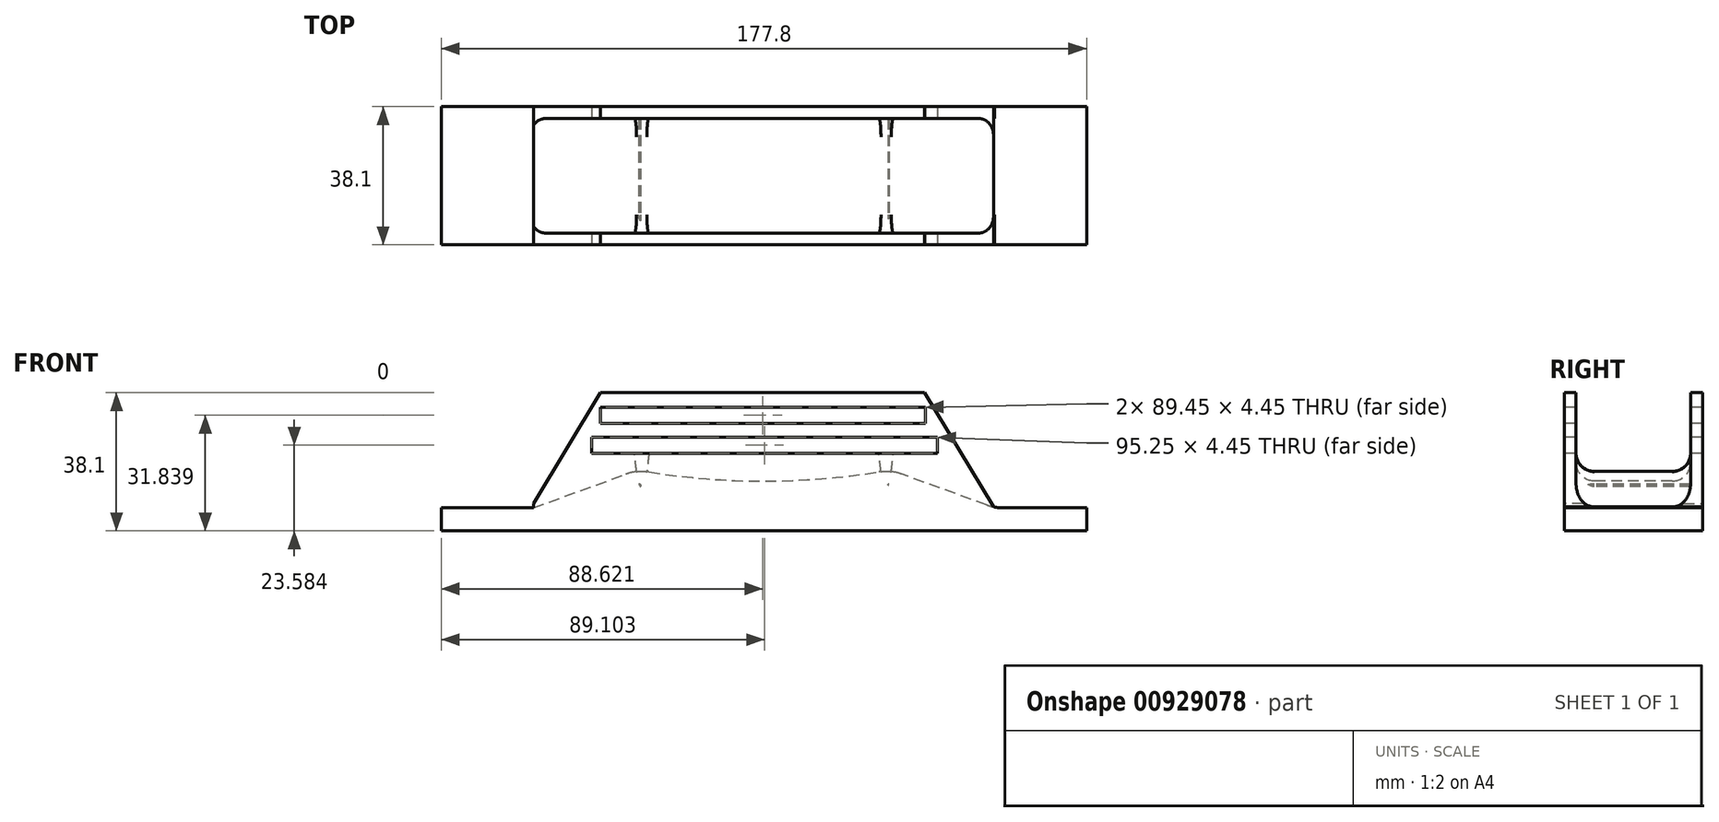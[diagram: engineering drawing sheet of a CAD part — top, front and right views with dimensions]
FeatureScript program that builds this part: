
annotation { "Feature Type Name" : "Feature", "Feature Type Description" : "" }
export const myFeature = defineFeature(function(context is Context, id is Id, definition is map)
    precondition{}
    {
        {
            var Q0;
            Q0=qCreatedBy(makeId("Top.planeOp"),FACE);
            var sketch = newSketch(context, id + "F0", { "sketchPlane" : qUnion([Q0])});
            skLineSegment(sketch, "E0.bottom", {"start": v(-37.6, 21.46) * mm, "end": v(140.2, 21.46) * mm});
            skLineSegment(sketch, "E0.top", {"start": v(-37.6, -16.64) * mm, "end": v(140.2, -16.64) * mm});
            skLineSegment(sketch, "E0.left", {"start": v(-37.6, 21.46) * mm, "end": v(-37.6, -16.64) * mm});
            skLineSegment(sketch, "E0.right", {"start": v(140.2, 21.46) * mm, "end": v(140.2, -16.64) * mm});
            skSolve(sketch);
        }
        {
            var Q0;
            Q0 = qSketchRegion(id + "F0", true);
            extrude(context, id + "F1", {"entities" : qUnion([Q0]), "depth" : 6.35 * mm, "offsetDistance" : 25.4 * mm});
        }
        {
            var Q0;
            Q0=makeQuery(id+"F1.opExtrude","SWEPT_FACE",FACE,{"disambiguationData":[OSD([sQuery(id+"F0.wireOp",EDGE,"E0.top")])]});
            var sketch = newSketch(context, id + "F2", { "sketchPlane" : qUnion([Q0])});
            skLineSegment(sketch, "E1", {"start": v(-12.2, 6.35) * mm, "end": v(16.44, 16.77) * mm});
            skLineSegment(sketch, "E2", {"start": v(114.8, 6.35) * mm, "end": v(86.15, 16.77) * mm});
            skLineSegment(sketch, "E3", {"start": v(16.44, 16.77) * mm, "end": v(17.74, 13.2) * mm});
            skLineSegment(sketch, "E4", {"start": v(17.74, 13.2) * mm, "end": v(-1.06, 6.35) * mm});
            skLineSegment(sketch, "E5", {"start": v(86.15, 16.77) * mm, "end": v(84.85, 13.2) * mm});
            skLineSegment(sketch, "E6", {"start": v(84.85, 13.2) * mm, "end": v(103.66, 6.35) * mm});
            skSolve(sketch);
        }
        {
            var Q0;
            {var subQ0=sQuery(id+"F0.wireOp",EDGE,"E0.top");Q0=makeQuery(id+"F4.boolean.opBoolean","MERGE",FACE,{"derivedFrom":[makeQuery(id+"F1.opExtrude","SWEPT_FACE",FACE,{"disambiguationData":[OSD([subQ0])]}),makeQuery(id+"F4.opExtrude","CAP_FACE",FACE,{"disambiguationData":[OSD([subQ0,sQuery(id+"F2.wireOp",EDGE,"E1"),sQuery(id+"F2.wireOp",EDGE,"E3"),sQuery(id+"F2.wireOp",EDGE,"E4")])],"isStart":true}),makeQuery(id+"F4.opExtrude","CAP_FACE",FACE,{"disambiguationData":[OSD([subQ0,sQuery(id+"F2.wireOp",EDGE,"E2"),sQuery(id+"F2.wireOp",EDGE,"E5"),sQuery(id+"F2.wireOp",EDGE,"E6")])],"isStart":true})]});}
            var sketch = newSketch(context, id + "F3", { "sketchPlane" : qUnion([Q0])});
            skArc(sketch, "E7", {"start": v(16.44, 16.77) * mm, "mid": v(51.3, 13.7) * mm, "end": v(86.15, 16.77) * mm});
            skLineSegment(sketch, "E8", {"start": v(16.44, 16.77) * mm, "end": v(16.44, 12.96) * mm});
            skLineSegment(sketch, "E9", {"start": v(86.15, 16.77) * mm, "end": v(86.15, 12.96) * mm});
            skArc(sketch, "E10", {"start": v(16.44, 12.96) * mm, "mid": v(51.3, 9.18) * mm, "end": v(86.15, 12.96) * mm});
            skSolve(sketch);
        }
        {
            var Q0;
            {var subQ0=sQuery(id+"F2.wireOp",EDGE,"E1");Q0=makeQuery(id+"F2.imprint","IMPRINT",FACE,{"disambiguationData":[TD([[makeQuery(id+"F2.imprint","IMPRINT",EDGE,{"derivedFrom":subQ0}),-1.0]])]});}
            var Q1;
            {var subQ0=sQuery(id+"F2.wireOp",EDGE,"E2");Q1=makeQuery(id+"F2.imprint","IMPRINT",FACE,{"disambiguationData":[TD([[makeQuery(id+"F2.imprint","IMPRINT",EDGE,{"derivedFrom":subQ0}),1.0]])]});}
            var Q2;
            Q2=makeQuery(id+"F3.imprint","IMPRINT",FACE,{"disambiguationData":[TD([[makeQuery(id+"F3.imprint","IMPRINT",EDGE,{"derivedFrom":sQuery(id+"F3.wireOp",EDGE,"E7")}),-1.0]])]});
            extrude(context, id + "F4", {"entities" : qUnion([Q0, Q1, Q2]), "operationType" : NewBodyOperationType.ADD, "oppositeDirection" : true, "depth" : 38.1 * mm, "offsetDistance" : 25.4 * mm});
        }
        {
            var Q0;
            Q0=makeQuery(id+"F4.opExtrude","SWEPT_EDGE",EDGE,{"disambiguationData":[OSD([sQuery(id+"F0.wireOp",EDGE,"E0.top"),sQuery(id+"F2.wireOp",EDGE,"E1")])]});
            var Q1;
            Q1=makeQuery(id+"F4.opExtrude","SWEPT_EDGE",EDGE,{"disambiguationData":[OSD([sQuery(id+"F0.wireOp",EDGE,"E0.top"),sQuery(id+"F2.wireOp",EDGE,"E2")])]});
            var Q2;
            Q2=makeQuery(id+"F4.opExtrude","SWEPT_EDGE",EDGE,{"disambiguationData":[OSD([sQuery(id+"F0.wireOp",EDGE,"E0.top"),sQuery(id+"F2.wireOp",EDGE,"E6")])]});
            var Q3;
            Q3=makeQuery(id+"F4.opExtrude","SWEPT_EDGE",EDGE,{"disambiguationData":[OSD([sQuery(id+"F0.wireOp",EDGE,"E0.top"),sQuery(id+"F2.wireOp",EDGE,"E4")])]});
            var Q4;
            Q4=makeQuery(id+"F4.boolean.opBoolean","MERGE",EDGE,{"derivedFrom":[makeQuery(id+"F4.opExtrude","SWEPT_EDGE",EDGE,{"disambiguationData":[OSD([sQuery(id+"F2.wireOp",EDGE,"E2"),sQuery(id+"F2.wireOp",EDGE,"E5")])]}),makeQuery(id+"F4.opExtrude","SWEPT_EDGE",EDGE,{"disambiguationData":[OSD([sQuery(id+"F3.wireOp",EDGE,"E7"),sQuery(id+"F3.wireOp",EDGE,"E9")])]})]});
            var Q5;
            Q5=makeQuery(id+"F4.boolean.opBoolean","MERGE",EDGE,{"derivedFrom":[makeQuery(id+"F4.opExtrude","SWEPT_EDGE",EDGE,{"disambiguationData":[OSD([sQuery(id+"F2.wireOp",EDGE,"E1"),sQuery(id+"F2.wireOp",EDGE,"E3")])]}),makeQuery(id+"F4.opExtrude","SWEPT_EDGE",EDGE,{"disambiguationData":[OSD([sQuery(id+"F3.wireOp",EDGE,"E7"),sQuery(id+"F3.wireOp",EDGE,"E8")])]})]});
            fillet(context, id + "F5", {"entities" : qUnion([Q0, Q1, Q2, Q3, Q4, Q5]), "radius" : 12.7 * mm, "tangentPropagation" : true, "allowEdgeOverflow" : false});
        }
        {
            var Q0;
            Q0=qCreatedBy(makeId("Top.planeOp"),FACE);
            var sketch = newSketch(context, id + "F6", { "sketchPlane" : qUnion([Q0])});
            skLineSegment(sketch, "E11.bottom", {"start": v(-12.2, 21.46) * mm, "end": v(114.8, 21.46) * mm});
            skLineSegment(sketch, "E11.top", {"start": v(-12.2, 18.2) * mm, "end": v(114.8, 18.2) * mm});
            skLineSegment(sketch, "E11.left", {"start": v(-12.2, 21.46) * mm, "end": v(-12.2, 18.2) * mm});
            skLineSegment(sketch, "E11.right", {"start": v(114.8, 21.46) * mm, "end": v(114.8, 18.2) * mm});
            skLineSegment(sketch, "E12.bottom", {"start": v(-12.2, -16.64) * mm, "end": v(114.8, -16.64) * mm});
            skLineSegment(sketch, "E12.top", {"start": v(-12.2, -13.38) * mm, "end": v(114.8, -13.38) * mm});
            skLineSegment(sketch, "E12.left", {"start": v(-12.2, -16.64) * mm, "end": v(-12.2, -13.38) * mm});
            skLineSegment(sketch, "E12.right", {"start": v(114.8, -16.64) * mm, "end": v(114.8, -13.38) * mm});
            skSolve(sketch);
        }
        {
            var Q0;
            Q0 = qSketchRegion(id + "F6", true);
            extrude(context, id + "F7", {"entities" : qUnion([Q0]), "operationType" : NewBodyOperationType.ADD, "depth" : 38.1 * mm, "offsetDistance" : 25.4 * mm});
        }
        {
            var Q0;
            Q0=qCreatedBy(makeId("Front.planeOp"),FACE);
            var sketch = newSketch(context, id + "F8", { "sketchPlane" : qUnion([Q0])});
            skLineSegment(sketch, "E13", {"start": v(-12.75, 6.58) * mm, "end": v(6.3, 38.1) * mm});
            skLineSegment(sketch, "E14", {"start": v(6.3, 38.1) * mm, "end": v(95.55, 38.1) * mm});
            skLineSegment(sketch, "E15", {"start": v(95.55, 38.1) * mm, "end": v(114.6, 6.58) * mm});
            skLineSegment(sketch, "E16", {"start": v(114.6, 6.58) * mm, "end": v(148.12, 6.58) * mm});
            skLineSegment(sketch, "E17", {"start": v(148.12, 6.58) * mm, "end": v(104.98, 72.7) * mm});
            skLineSegment(sketch, "E18", {"start": v(104.98, 72.7) * mm, "end": v(-3.95, 64.2) * mm});
            skLineSegment(sketch, "E19", {"start": v(-3.95, 64.2) * mm, "end": v(-37.6, 6.36) * mm});
            skLineSegment(sketch, "E20", {"start": v(-37.6, 6.36) * mm, "end": v(-12.75, 6.58) * mm});
            skSolve(sketch);
        }
        {
            var Q0;
            Q0=makeQuery(id+"F8.imprint","IMPRINT",FACE,{"disambiguationData":[TD([[makeQuery(id+"F8.imprint","IMPRINT",EDGE,{"derivedFrom":sQuery(id+"F8.wireOp",EDGE,"E13")}),1.0]])]});
            extrude(context, id + "F9", {"entities" : qUnion([Q0]), "operationType" : NewBodyOperationType.REMOVE, "endBound" : BoundingType.SYMMETRIC, "oppositeDirection" : true, "depth" : 254 * mm, "offsetDistance" : 25.4 * mm});
        }
        {
            var Q0;
            {var subQ0=sQuery(id+"F0.wireOp",EDGE,"E0.top");Q0=makeQuery(id+"F7.boolean.opBoolean","MERGE",FACE,{"derivedFrom":[makeQuery(id+"F4.boolean.opBoolean","MERGE",FACE,{"derivedFrom":[makeQuery(id+"F1.opExtrude","SWEPT_FACE",FACE,{"disambiguationData":[OSD([subQ0])]}),makeQuery(id+"F4.opExtrude","CAP_FACE",FACE,{"disambiguationData":[OSD([subQ0,sQuery(id+"F2.wireOp",EDGE,"E1"),sQuery(id+"F2.wireOp",EDGE,"E3"),sQuery(id+"F2.wireOp",EDGE,"E4")])],"isStart":true}),makeQuery(id+"F4.opExtrude","CAP_FACE",FACE,{"disambiguationData":[OSD([subQ0,sQuery(id+"F2.wireOp",EDGE,"E2"),sQuery(id+"F2.wireOp",EDGE,"E5"),sQuery(id+"F2.wireOp",EDGE,"E6")])],"isStart":true}),makeQuery(id+"F4.opExtrude","CAP_FACE",FACE,{"disambiguationData":[OSD([sQuery(id+"F3.wireOp",EDGE,"E7"),sQuery(id+"F3.wireOp",EDGE,"E8"),sQuery(id+"F3.wireOp",EDGE,"E9"),sQuery(id+"F3.wireOp",EDGE,"E10")])],"isStart":true})]}),makeQuery(id+"F7.opExtrude","SWEPT_FACE",FACE,{"disambiguationData":[OSD([sQuery(id+"F6.wireOp",EDGE,"E12.bottom")])]})]});}
            var sketch = newSketch(context, id + "F10", { "sketchPlane" : qUnion([Q0])});
            skLineSegment(sketch, "E21.bottom", {"start": v(6.3, 34.06) * mm, "end": v(95.74, 34.06) * mm});
            skLineSegment(sketch, "E21.top", {"start": v(6.3, 29.62) * mm, "end": v(95.74, 29.62) * mm});
            skLineSegment(sketch, "E21.left", {"start": v(6.3, 34.06) * mm, "end": v(6.3, 29.62) * mm});
            skLineSegment(sketch, "E21.right", {"start": v(95.74, 34.06) * mm, "end": v(95.74, 29.62) * mm});
            skSolve(sketch);
        }
        {
            var Q0;
            Q0 = qSketchRegion(id + "F10", true);
            extrude(context, id + "F11", {"entities" : qUnion([Q0]), "operationType" : NewBodyOperationType.REMOVE, "oppositeDirection" : true, "depth" : 254 * mm, "offsetDistance" : 25.4 * mm});
        }
        {
            var Q0;
            {var subQ0=sQuery(id+"F0.wireOp",EDGE,"E0.top");Q0=makeQuery(id+"F7.boolean.opBoolean","MERGE",FACE,{"derivedFrom":[makeQuery(id+"F4.boolean.opBoolean","MERGE",FACE,{"derivedFrom":[makeQuery(id+"F1.opExtrude","SWEPT_FACE",FACE,{"disambiguationData":[OSD([subQ0])]}),makeQuery(id+"F4.opExtrude","CAP_FACE",FACE,{"disambiguationData":[OSD([subQ0,sQuery(id+"F2.wireOp",EDGE,"E1"),sQuery(id+"F2.wireOp",EDGE,"E3"),sQuery(id+"F2.wireOp",EDGE,"E4")])],"isStart":true}),makeQuery(id+"F4.opExtrude","CAP_FACE",FACE,{"disambiguationData":[OSD([subQ0,sQuery(id+"F2.wireOp",EDGE,"E2"),sQuery(id+"F2.wireOp",EDGE,"E5"),sQuery(id+"F2.wireOp",EDGE,"E6")])],"isStart":true}),makeQuery(id+"F4.opExtrude","CAP_FACE",FACE,{"disambiguationData":[OSD([sQuery(id+"F3.wireOp",EDGE,"E7"),sQuery(id+"F3.wireOp",EDGE,"E8"),sQuery(id+"F3.wireOp",EDGE,"E9"),sQuery(id+"F3.wireOp",EDGE,"E10")])],"isStart":true})]}),makeQuery(id+"F7.opExtrude","SWEPT_FACE",FACE,{"disambiguationData":[OSD([sQuery(id+"F6.wireOp",EDGE,"E12.bottom")])]})]});}
            var sketch = newSketch(context, id + "F12", { "sketchPlane" : qUnion([Q0])});
            skLineSegment(sketch, "E22.bottom", {"start": v(3.88, 21.36) * mm, "end": v(99.13, 21.36) * mm});
            skLineSegment(sketch, "E22.top", {"start": v(3.88, 25.8) * mm, "end": v(99.13, 25.8) * mm});
            skLineSegment(sketch, "E22.left", {"start": v(3.88, 21.36) * mm, "end": v(3.88, 25.8) * mm});
            skLineSegment(sketch, "E22.right", {"start": v(99.13, 21.36) * mm, "end": v(99.13, 25.8) * mm});
            skSolve(sketch);
        }
        {
            var Q0;
            Q0 = qSketchRegion(id + "F12", true);
            extrude(context, id + "F13", {"entities" : qUnion([Q0]), "operationType" : NewBodyOperationType.REMOVE, "oppositeDirection" : true, "depth" : 254 * mm, "offsetDistance" : 25.4 * mm});
        }
        {
            var Q0;
            Q0=makeQuery(id+"F7.boolean.opBoolean","INTERSECT",EDGE,{"derivedFrom":[makeQuery(id+"F4.opExtrude","SWEPT_FACE",FACE,{"disambiguationData":[OSD([sQuery(id+"F2.wireOp",EDGE,"E2")])]}),makeQuery(id+"F7.opExtrude","SWEPT_FACE",FACE,{"disambiguationData":[OSD([sQuery(id+"F6.wireOp",EDGE,"E11.top")])]})]});
            var Q1;
            Q1=makeQuery(id+"F7.boolean.opBoolean","INTERSECT",EDGE,{"derivedFrom":[makeQuery(id+"F4.opExtrude","SWEPT_FACE",FACE,{"disambiguationData":[OSD([sQuery(id+"F3.wireOp",EDGE,"E7")])]}),makeQuery(id+"F7.opExtrude","SWEPT_FACE",FACE,{"disambiguationData":[OSD([sQuery(id+"F6.wireOp",EDGE,"E11.top")])]})]});
            var Q2;
            Q2=makeQuery(id+"F7.boolean.opBoolean","INTERSECT",EDGE,{"derivedFrom":[makeQuery(id+"F5.opFillet","BLEND_FACE",FACE,{"disambiguationData":[OSD([sQuery(id+"F2.wireOp",EDGE,"E2"),sQuery(id+"F2.wireOp",EDGE,"E5"),sQuery(id+"F3.wireOp",EDGE,"E7"),sQuery(id+"F3.wireOp",EDGE,"E9")])]}),makeQuery(id+"F7.opExtrude","SWEPT_FACE",FACE,{"disambiguationData":[OSD([sQuery(id+"F6.wireOp",EDGE,"E11.top")])]})]});
            var Q3;
            Q3=makeQuery(id+"F7.boolean.opBoolean","INTERSECT",EDGE,{"derivedFrom":[makeQuery(id+"F4.opExtrude","SWEPT_FACE",FACE,{"disambiguationData":[OSD([sQuery(id+"F2.wireOp",EDGE,"E2")])]}),makeQuery(id+"F7.opExtrude","SWEPT_FACE",FACE,{"disambiguationData":[OSD([sQuery(id+"F6.wireOp",EDGE,"E12.top")])]})]});
            var Q4;
            Q4=makeQuery(id+"F7.boolean.opBoolean","INTERSECT",EDGE,{"derivedFrom":[makeQuery(id+"F5.opFillet","BLEND_FACE",FACE,{"disambiguationData":[OSD([sQuery(id+"F2.wireOp",EDGE,"E2"),sQuery(id+"F2.wireOp",EDGE,"E5"),sQuery(id+"F3.wireOp",EDGE,"E7"),sQuery(id+"F3.wireOp",EDGE,"E9")])]}),makeQuery(id+"F7.opExtrude","SWEPT_FACE",FACE,{"disambiguationData":[OSD([sQuery(id+"F6.wireOp",EDGE,"E12.top")])]})]});
            var Q5;
            Q5=makeQuery(id+"F7.boolean.opBoolean","INTERSECT",EDGE,{"derivedFrom":[makeQuery(id+"F4.opExtrude","SWEPT_FACE",FACE,{"disambiguationData":[OSD([sQuery(id+"F3.wireOp",EDGE,"E7")])]}),makeQuery(id+"F7.opExtrude","SWEPT_FACE",FACE,{"disambiguationData":[OSD([sQuery(id+"F6.wireOp",EDGE,"E12.top")])]})]});
            var Q6;
            Q6=makeQuery(id+"F7.boolean.opBoolean","INTERSECT",EDGE,{"derivedFrom":[makeQuery(id+"F4.opExtrude","SWEPT_FACE",FACE,{"disambiguationData":[OSD([sQuery(id+"F2.wireOp",EDGE,"E1")])]}),makeQuery(id+"F7.opExtrude","SWEPT_FACE",FACE,{"disambiguationData":[OSD([sQuery(id+"F6.wireOp",EDGE,"E11.top")])]})]});
            var Q7;
            Q7=makeQuery(id+"F7.boolean.opBoolean","INTERSECT",EDGE,{"derivedFrom":[makeQuery(id+"F5.opFillet","BLEND_FACE",FACE,{"disambiguationData":[OSD([sQuery(id+"F2.wireOp",EDGE,"E1"),sQuery(id+"F2.wireOp",EDGE,"E3"),sQuery(id+"F3.wireOp",EDGE,"E7"),sQuery(id+"F3.wireOp",EDGE,"E8")])]}),makeQuery(id+"F7.opExtrude","SWEPT_FACE",FACE,{"disambiguationData":[OSD([sQuery(id+"F6.wireOp",EDGE,"E11.top")])]})]});
            var Q8;
            Q8=makeQuery(id+"F7.boolean.opBoolean","INTERSECT",EDGE,{"derivedFrom":[makeQuery(id+"F4.opExtrude","SWEPT_FACE",FACE,{"disambiguationData":[OSD([sQuery(id+"F2.wireOp",EDGE,"E1")])]}),makeQuery(id+"F7.opExtrude","SWEPT_FACE",FACE,{"disambiguationData":[OSD([sQuery(id+"F6.wireOp",EDGE,"E12.top")])]})]});
            var Q9;
            Q9=makeQuery(id+"F7.boolean.opBoolean","INTERSECT",EDGE,{"derivedFrom":[makeQuery(id+"F5.opFillet","BLEND_FACE",FACE,{"disambiguationData":[OSD([sQuery(id+"F2.wireOp",EDGE,"E1"),sQuery(id+"F2.wireOp",EDGE,"E3"),sQuery(id+"F3.wireOp",EDGE,"E7"),sQuery(id+"F3.wireOp",EDGE,"E8")])]}),makeQuery(id+"F7.opExtrude","SWEPT_FACE",FACE,{"disambiguationData":[OSD([sQuery(id+"F6.wireOp",EDGE,"E12.top")])]})]});
            var Q10;
            Q10=makeQuery(id+"F7.boolean.opBoolean","INTERSECT",EDGE,{"derivedFrom":[makeQuery(id+"F5.opFillet","BLEND_FACE",FACE,{"disambiguationData":[OSD([sQuery(id+"F0.wireOp",EDGE,"E0.top"),sQuery(id+"F2.wireOp",EDGE,"E1")])]}),makeQuery(id+"F7.opExtrude","SWEPT_FACE",FACE,{"disambiguationData":[OSD([sQuery(id+"F6.wireOp",EDGE,"E12.top")])]})]});
            fillet(context, id + "F14", {"entities" : qUnion([Q0, Q1, Q2, Q3, Q4, Q5, Q6, Q7, Q8, Q9, Q10]), "radius" : 5.08 * mm, "tangentPropagation" : true, "allowEdgeOverflow" : false});
        }
        {
            var Q0;
            {var subQ0=sQuery(id+"F0.wireOp",EDGE,"E0.top");Q0=makeQuery(id+"F7.boolean.opBoolean","MERGE",FACE,{"derivedFrom":[makeQuery(id+"F4.boolean.opBoolean","MERGE",FACE,{"derivedFrom":[makeQuery(id+"F1.opExtrude","SWEPT_FACE",FACE,{"disambiguationData":[OSD([sQuery(id+"F0.wireOp",EDGE,"E0.bottom")])]}),makeQuery(id+"F4.opExtrude","CAP_FACE",FACE,{"disambiguationData":[OSD([subQ0,sQuery(id+"F2.wireOp",EDGE,"E1"),sQuery(id+"F2.wireOp",EDGE,"E3"),sQuery(id+"F2.wireOp",EDGE,"E4")])],"isStart":false}),makeQuery(id+"F4.opExtrude","CAP_FACE",FACE,{"disambiguationData":[OSD([subQ0,sQuery(id+"F2.wireOp",EDGE,"E2"),sQuery(id+"F2.wireOp",EDGE,"E5"),sQuery(id+"F2.wireOp",EDGE,"E6")])],"isStart":false}),makeQuery(id+"F4.opExtrude","CAP_FACE",FACE,{"disambiguationData":[OSD([sQuery(id+"F3.wireOp",EDGE,"E7"),sQuery(id+"F3.wireOp",EDGE,"E8"),sQuery(id+"F3.wireOp",EDGE,"E9"),sQuery(id+"F3.wireOp",EDGE,"E10")])],"isStart":false})]}),makeQuery(id+"F7.opExtrude","SWEPT_FACE",FACE,{"disambiguationData":[OSD([sQuery(id+"F6.wireOp",EDGE,"E11.bottom")])]})]});}
            var sketch = newSketch(context, id + "F15", { "sketchPlane" : qUnion([Q0])});
            skLineSegment(sketch, "E23.bottom", {"start": v(-17.25, 13.1) * mm, "end": v(-85.54, 13.1) * mm});
            skLineSegment(sketch, "E23.top", {"start": v(-17.25, 3.9) * mm, "end": v(-85.54, 3.9) * mm});
            skLineSegment(sketch, "E23.left", {"start": v(-17.25, 13.1) * mm, "end": v(-17.25, 3.9) * mm});
            skLineSegment(sketch, "E23.right", {"start": v(-85.54, 13.1) * mm, "end": v(-85.54, 3.9) * mm});
            skSolve(sketch);
        }
        {
            var Q0;
            Q0 = qSketchRegion(id + "F15", true);
            extrude(context, id + "F16", {"entities" : qUnion([Q0]), "operationType" : NewBodyOperationType.ADD, "oppositeDirection" : true, "depth" : 38.1 * mm, "offsetDistance" : 25.4 * mm});
        }
    });
